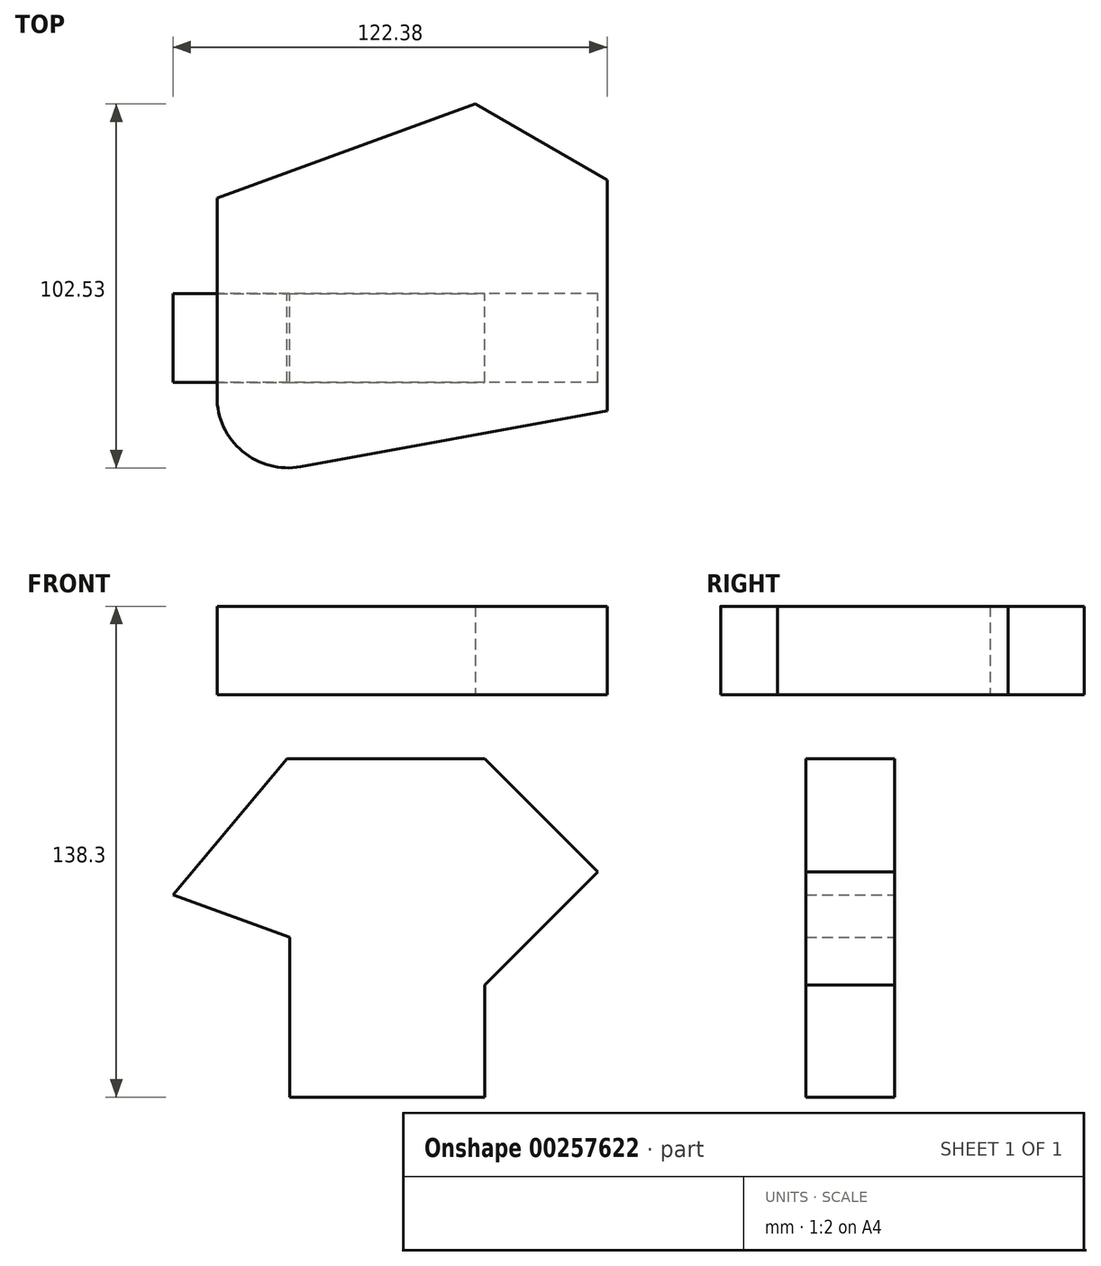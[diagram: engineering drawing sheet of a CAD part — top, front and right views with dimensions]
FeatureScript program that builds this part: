
annotation { "Feature Type Name" : "Feature", "Feature Type Description" : "" }
export const myFeature = defineFeature(function(context is Context, id is Id, definition is map)
    precondition{}
    {
        {
            var Q0;
            Q0=qCreatedBy(makeId("Top.planeOp"),FACE);
            var sketch = newSketch(context, id + "F0", { "sketchPlane" : qUnion([Q0])});
            skLineSegment(sketch, "E0", {"start": v(89.49, 31.98) * mm, "end": v(89.49, -33.02) * mm});
            skLineSegment(sketch, "E1", {"start": v(-20.51, -33.02) * mm, "end": v(-20.51, 26.98) * mm});
            skLineSegment(sketch, "E2", {"start": v(89.49, 31.98) * mm, "end": v(52.27, 53.47) * mm});
            skLineSegment(sketch, "E3", {"start": v(-20.51, 26.98) * mm, "end": v(52.27, 53.47) * mm});
            skLineSegment(sketch, "E4", {"start": v(-20.51, -29.06) * mm, "end": v(-20.51, -33.02) * mm});
            skLineSegment(sketch, "E5", {"start": v(3.07, -48.74) * mm, "end": v(89.49, -33.02) * mm});
            skPoint(sketch, "E6.visualSharp", {"position": v(-20.51, -53.02) * mm});
            skArc(sketch, "E6.filletArc", {"start": v(-20.51, -29.06) * mm, "mid": v(-13.33, -44.41) * mm, "end": v(3.07, -48.74) * mm});
            skSolve(sketch);
        }
        {
            var Q0;
            Q0=makeQuery(id+"F0.imprint","IMPRINT",FACE,{"disambiguationData":[TD([[makeQuery(id+"F0.imprint","IMPRINT",EDGE,{"derivedFrom":sQuery(id+"F0.wireOp",EDGE,"E0")}),-1.0]])]});
            extrude(context, id + "F1", {"entities" : qUnion([Q0]), "depth" : 25 * mm});
        }
        {
            var Q0;
            Q0=qCreatedBy(makeId("Front.planeOp"),FACE);
            var sketch = newSketch(context, id + "F2", { "sketchPlane" : qUnion([Q0])});
            skLineSegment(sketch, "E7", {"start": v(55, -113.3) * mm, "end": v(0, -113.3) * mm});
            skLineSegment(sketch, "E8", {"start": v(0, -113.3) * mm, "end": v(0, -68.3) * mm});
            skLineSegment(sketch, "E9", {"start": v(0, -68.3) * mm, "end": v(-32.89, -56.33) * mm});
            skLineSegment(sketch, "E10", {"start": v(-32.89, -56.33) * mm, "end": v(-0.75, -18.03) * mm});
            skPoint(sketch, "E11.end.orphan", {"position": v(55, -81.67) * mm});
            skPoint(sketch, "E12.end.orphan", {"position": v(54.25, -81.67) * mm});
            skLineSegment(sketch, "E13", {"start": v(-0.75, -18.03) * mm, "end": v(55, -18.03) * mm});
            skLineSegment(sketch, "E14", {"start": v(55, -18.03) * mm, "end": v(86.82, -49.85) * mm});
            skLineSegment(sketch, "E15", {"start": v(86.82, -49.85) * mm, "end": v(55, -81.67) * mm});
            skLineSegment(sketch, "E16", {"start": v(55, -81.67) * mm, "end": v(55, -113.3) * mm});
            skSolve(sketch);
        }
        {
            var Q0;
            Q0 = qSketchRegion(id + "F2", true);
            extrude(context, id + "F3", {"entities" : qUnion([Q0]), "depth" : 25 * mm});
        }
    });
